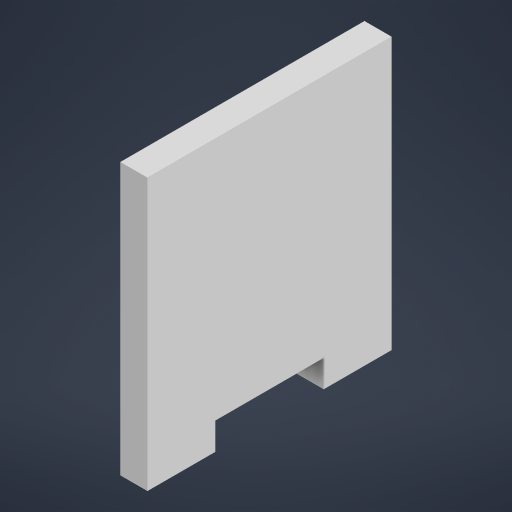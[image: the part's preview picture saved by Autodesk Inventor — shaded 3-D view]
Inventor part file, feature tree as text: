
AUTODESK INVENTOR PART (.ipt)
format: ipt  version: 2023.2 (Build 272271000, 271)  size: 280,576 bytes
history: native  units: mm
features: sketch x1
ambient origin geometry x8: Origin, YZ Plane, XZ Plane, XY Plane, X Axis, Y Axis, Z Axis, Center Point
bodies: Body1 (feature_tree)
feature tree (1):
  sketch  "Sketch1"  dims[d228=4.0mm d229=36.0mm d230=36.0mm d231=36.0mm d232=10.0mm d233=10.0mm d234=4.0mm d235=0.0mm d9=0.5mm d10=0.872665mm d11=0.5mm d12=0.872665mm d13=0.5mm d14=0.872665mm d27=0.5mm d28=0.872665mm d29=0.5mm d30=0.872665mm d88=0.5mm d89=0.872665mm d90=0.5mm d91=0.872665mm d116=0.5mm d117=0.872665mm d118=0.5mm d119=0.872665mm d154=0.5mm d155=0.872665mm d156=0.5mm d157=0.872665mm d181=0.5mm d182=0.872665mm d183=0.5mm d184=0.872665mm d221=0.5mm d222=0.872665mm d223=0.5mm d224=0.872665mm]
